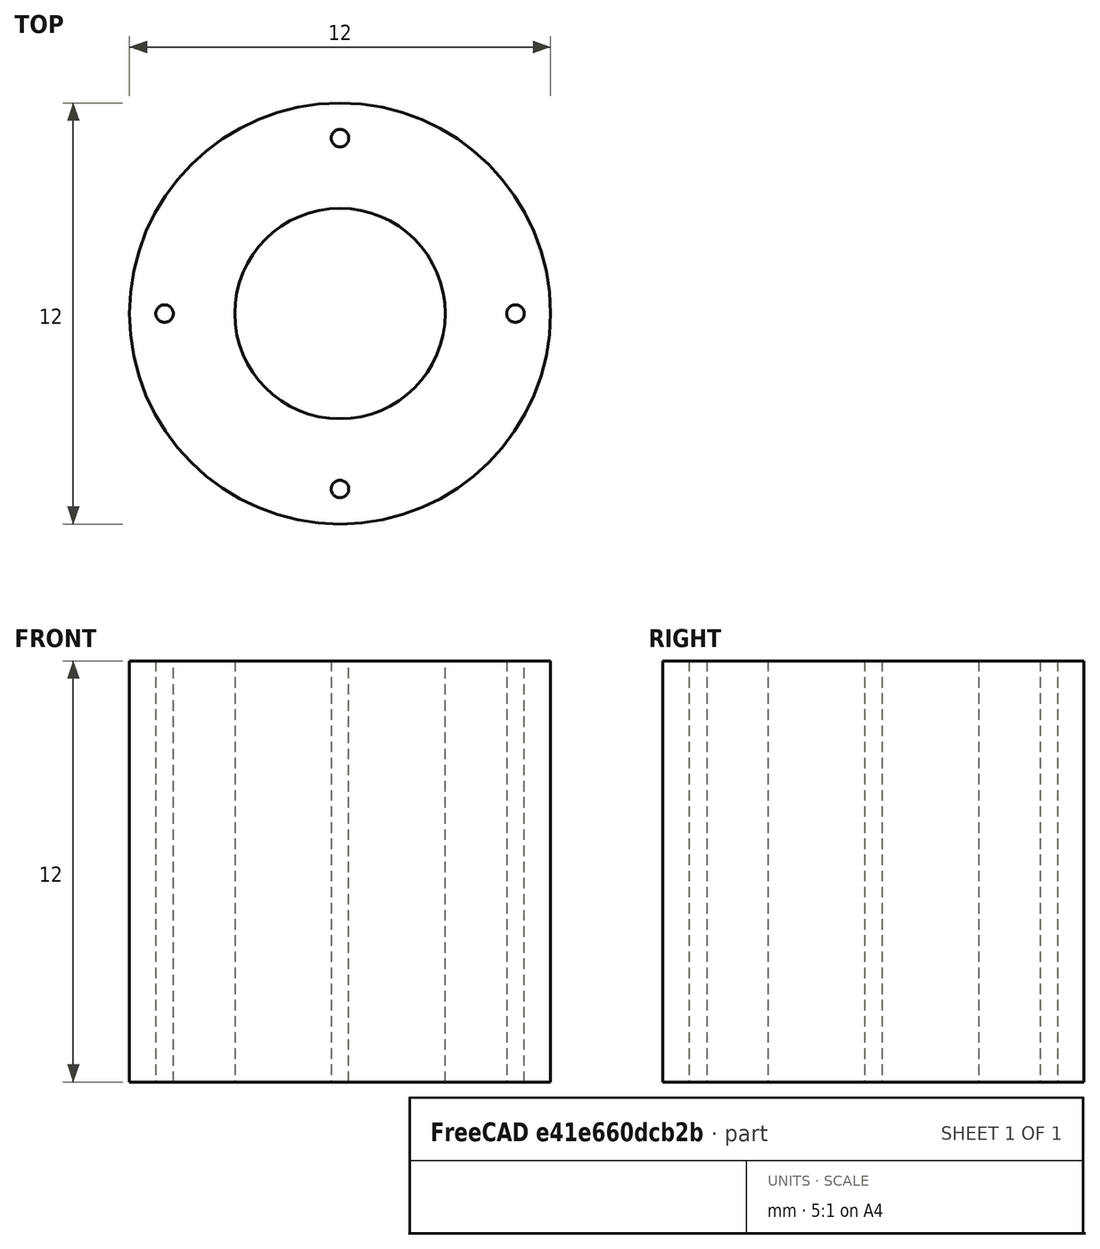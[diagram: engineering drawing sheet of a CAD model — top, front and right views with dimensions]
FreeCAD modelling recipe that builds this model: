
FCSTD DOCUMENT  (FreeCAD 0.17R13528 (Git))
Label: myrschraubenschkopfoderso
License: All rights reserved
LicenseURL: http://en.wikipedia.org/wiki/All_rights_reserved
objects: Sketcher::SketchObject×1, PartDesign::Pad×1, PartDesign::Body×1, App::Part×1
note: 4 computed .brp shape members not serialized (recipe doc carries the construction recipe); baked Part::Feature solids carry a one-line shape summary decoded from their .brp

FEATURE [Sketcher::SketchObject] Sketch
  sketch-geometry (7):
    g0: Circle CenterX=0 CenterY=0 CenterZ=0 NormalX=0 NormalY=0 NormalZ=1 AngleXU=0 Radius=6
    g1: Circle CenterX=0 CenterY=0 CenterZ=0 NormalX=0 NormalY=0 NormalZ=1 AngleXU=0 Radius=3
    g2: GeomPoint X=0 Y=0 Z=0
    g3: Circle CenterX=-5 CenterY=0 CenterZ=0 NormalX=0 NormalY=0 NormalZ=1 AngleXU=0 Radius=0.25
    g4: Circle CenterX=5 CenterY=0 CenterZ=0 NormalX=0 NormalY=0 NormalZ=1 AngleXU=0 Radius=0.25
    g5: Circle CenterX=0 CenterY=5 CenterZ=0 NormalX=0 NormalY=0 NormalZ=1 AngleXU=0 Radius=0.25
    g6: Circle CenterX=0 CenterY=-5 CenterZ=0 NormalX=0 NormalY=0 NormalZ=1 AngleXU=0 Radius=0.25
  constraints (19):
    c: Radius(g1) = 3
    c: Radius(g0) = 6
    c: Coincident(g2,g1)
    c: DistanceX(g0,g1) = 0
    c: DistanceY(g0,g1) = 0
    c: Radius(g3) = 0.25
    c: DistanceX(g3,g0) = 5
    c: Radius(g4) = 0.25
    c: DistanceX(g0,g4) = 5
    c: PointOnObject(g0,g-1)
    c: PointOnObject(g3,g-1)
    c: PointOnObject(g4,g-1)
    c: Radius(g5) = 0.25
    c: DistanceY(g0,g5) = 5
    c: PointOnObject(g5,g-2)
    c: Radius(g6) = 0.25
    c: DistanceY(g6,g-1) = 5
    c: PointOnObject(g6,g-2)
    c: PointOnObject(g0,g-2)
FEATURE [PartDesign::Pad] Pad
  Length = 12
  Length2 = 100
  Profile = -> Sketch
  Type = 0
FEATURE [PartDesign::Body] Body
  Group = -> [Sketch,Pad]
  Origin = -> Origin003
  Tip = -> Pad
FEATURE [App::Part] Part
  Group = -> [Body]
  License = CC BY 3.0
  LicenseURL = http://creativecommons.org/licenses/by/3.0/
  Origin = -> Origin
